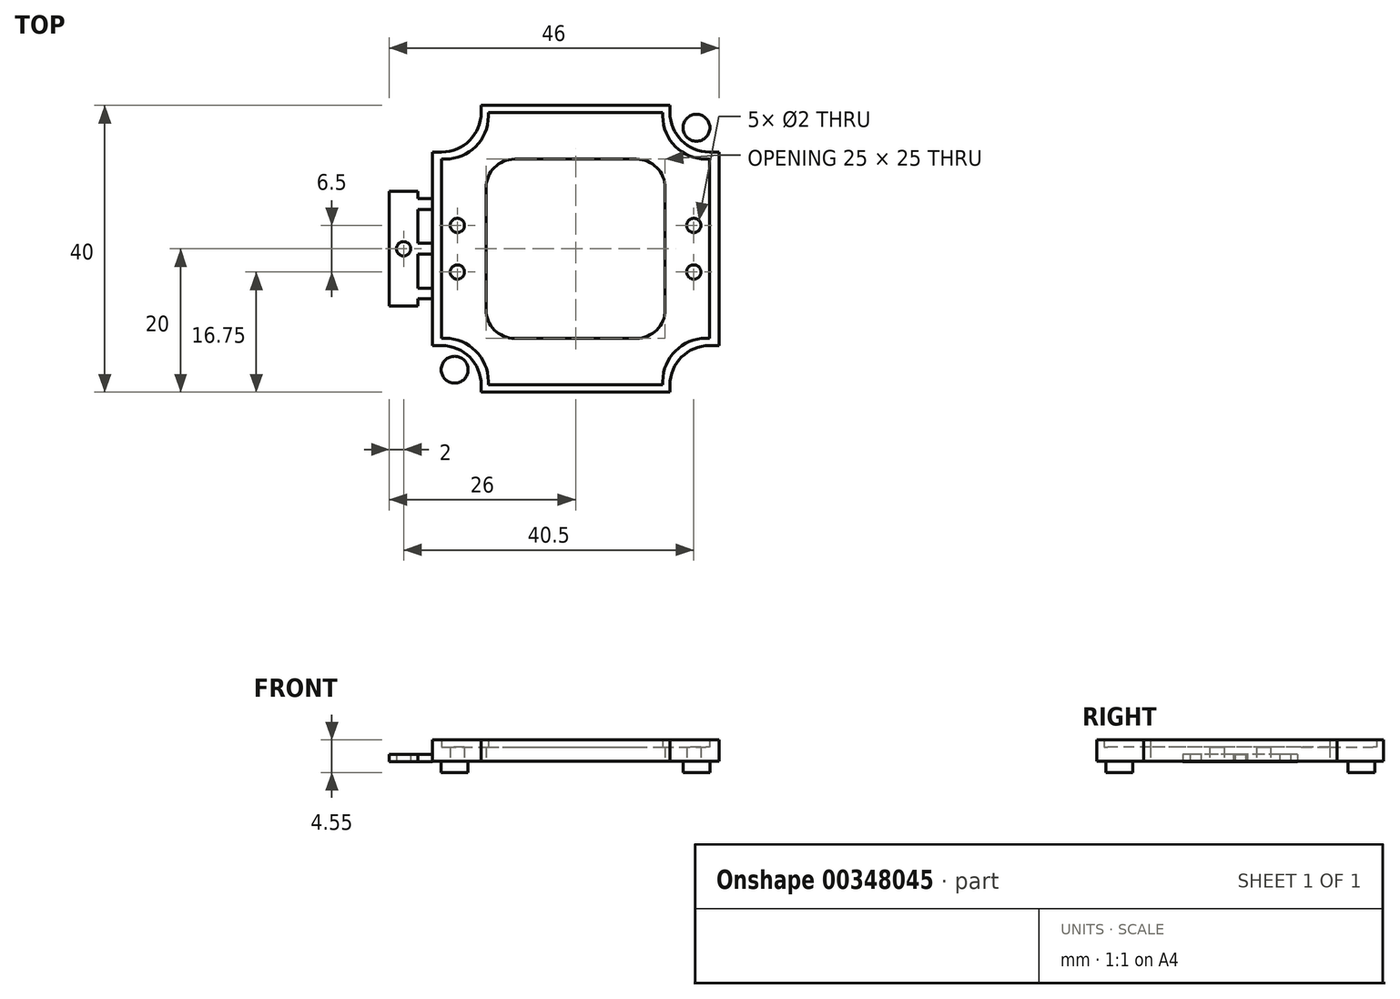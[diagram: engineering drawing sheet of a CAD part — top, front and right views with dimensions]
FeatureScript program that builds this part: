
annotation { "Feature Type Name" : "Feature", "Feature Type Description" : "" }
export const myFeature = defineFeature(function(context is Context, id is Id, definition is map)
    precondition{}
    {
        {
            var Q0;
            Q0=qCreatedBy(makeId("Top.planeOp"),FACE);
            var sketch = newSketch(context, id + "F0", { "sketchPlane" : qUnion([Q0])});
            skLineSegment(sketch, "E0.bottom", {"start": v(-20, 23) * mm, "end": v(20, 23) * mm});
            skLineSegment(sketch, "E0.top", {"start": v(-20, -23) * mm, "end": v(20, -23) * mm});
            skLineSegment(sketch, "E0.left", {"start": v(-20, 23) * mm, "end": v(-20, -23) * mm});
            skLineSegment(sketch, "E0.right", {"start": v(20, 23) * mm, "end": v(20, -23) * mm});
            skPoint(sketch, "E0.middle", {"position": v(0, 0) * mm});
            skLineSegment(sketch, "E1.bottom", {"start": v(-20, 7) * mm, "end": v(-22, 7) * mm});
            skLineSegment(sketch, "E1.top", {"start": v(-20, 5.5) * mm, "end": v(-22, 5.5) * mm});
            skLineSegment(sketch, "E1.left", {"start": v(-20, 7) * mm, "end": v(-20, 5.5) * mm});
            skLineSegment(sketch, "E2.bottom", {"start": v(-20, 0.75) * mm, "end": v(-22, 0.75) * mm});
            skLineSegment(sketch, "E2.top", {"start": v(-20, -0.75) * mm, "end": v(-22, -0.75) * mm});
            skLineSegment(sketch, "E2.left", {"start": v(-20, 0.75) * mm, "end": v(-20, -0.75) * mm});
            skLineSegment(sketch, "E3.MirrorCS", {"start": v(-20, -5.5) * mm, "end": v(-22, -5.5) * mm});
            skLineSegment(sketch, "E4.MirrorCS", {"start": v(-20, -7) * mm, "end": v(-22, -7) * mm});
            skLineSegment(sketch, "E5.bottom", {"start": v(-26, 8) * mm, "end": v(-22, 8) * mm});
            skLineSegment(sketch, "E5.top", {"start": v(-26, -8) * mm, "end": v(-22, -8) * mm});
            skLineSegment(sketch, "E5.left", {"start": v(-26, 8) * mm, "end": v(-26, -8) * mm});
            skLineSegment(sketch, "E5.right", {"start": v(-22, 8) * mm, "end": v(-22, 7) * mm});
            skCircle(sketch, "E6", {"center": v(-24, 0) * mm, "radius": 1 * mm});
            skLineSegment(sketch, "E7.MirrorCS", {"start": v(22, 0.75) * mm, "end": v(22, -0.75) * mm});
            skLineSegment(sketch, "E8.MirrorCS", {"start": v(20, 0.75) * mm, "end": v(20, -0.75) * mm});
            skLineSegment(sketch, "E9.MirrorCS", {"start": v(20, 7) * mm, "end": v(20, 5.5) * mm});
            skLineSegment(sketch, "E10.MirrorCS", {"start": v(22, 8) * mm, "end": v(22, 7) * mm});
            skLineSegment(sketch, "E11.MirrorCS", {"start": v(26, 8) * mm, "end": v(26, -8) * mm});
            skCircle(sketch, "E12.MirrorC", {"center": v(24, 0) * mm, "radius": 1 * mm});
            skLineSegment(sketch, "E13.MirrorCS", {"start": v(20, -0.75) * mm, "end": v(22, -0.75) * mm});
            skLineSegment(sketch, "E14.MirrorCS", {"start": v(26, -8) * mm, "end": v(22, -8) * mm});
            skLineSegment(sketch, "E15.MirrorCS", {"start": v(20, -5.5) * mm, "end": v(22, -5.5) * mm});
            skLineSegment(sketch, "E16.MirrorCS", {"start": v(20, 0.75) * mm, "end": v(22, 0.75) * mm});
            skLineSegment(sketch, "E17.MirrorCS", {"start": v(20, 7) * mm, "end": v(22, 7) * mm});
            skLineSegment(sketch, "E18.MirrorCS", {"start": v(20, -7) * mm, "end": v(22, -7) * mm});
            skLineSegment(sketch, "E19.MirrorCS", {"start": v(20, 5.5) * mm, "end": v(22, 5.5) * mm});
            skLineSegment(sketch, "E20.MirrorCS", {"start": v(26, 8) * mm, "end": v(22, 8) * mm});
            skLineSegment(sketch, "E21.trimOffspring", {"start": v(-22, 5.5) * mm, "end": v(-22, -5.5) * mm});
            skLineSegment(sketch, "E22.trimOffspring", {"start": v(-22, -7) * mm, "end": v(-22, -8) * mm});
            skPoint(sketch, "E23.MirrorCS.start.orphan", {"position": v(-22, -7) * mm});
            skLineSegment(sketch, "E24.trimOffspring", {"start": v(22, 5.5) * mm, "end": v(22, -5.5) * mm});
            skPoint(sketch, "E25.MirrorCS.end.orphan", {"position": v(22, -5.5) * mm});
            skPoint(sketch, "E25.MirrorCS.start.orphan", {"position": v(22, -7) * mm});
            skLineSegment(sketch, "E26.trimOffspring", {"start": v(22, -7) * mm, "end": v(22, -8) * mm});
            skSolve(sketch);
        }
        {
            var Q0;
            Q0=makeQuery(id+"F0.imprint","IMPRINT",FACE,{"disambiguationData":[TD([[makeQuery(id+"F0.imprint","IMPRINT",EDGE,{"derivedFrom":sQuery(id+"F0.wireOp",EDGE,"E0.bottom")}),-1.0]])]});
            extrude(context, id + "F1", {"entities" : qUnion([Q0]), "depth" : 1.55 * mm});
        }
        {
            var Q0;
            Q0=makeQuery(id+"F1.opExtrude","CAP_FACE",FACE,{"disambiguationData":[OSD([sQuery(id+"F0.wireOp",EDGE,"E0.bottom"),sQuery(id+"F0.wireOp",EDGE,"E0.top"),sQuery(id+"F0.wireOp",EDGE,"E0.left"),sQuery(id+"F0.wireOp",EDGE,"E0.right")])],"isStart":false});
            var sketch = newSketch(context, id + "F2", { "sketchPlane" : qUnion([Q0])});
            skLineSegment(sketch, "E27.bottom", {"start": v(-13.17, 20) * mm, "end": v(13.17, 20) * mm});
            skLineSegment(sketch, "E27.top", {"start": v(-13.17, -20) * mm, "end": v(13.17, -20) * mm});
            skLineSegment(sketch, "E27.left", {"start": v(-20, 13.5) * mm, "end": v(-20, -13.5) * mm});
            skLineSegment(sketch, "E27.right", {"start": v(20, 13.5) * mm, "end": v(20, -13.5) * mm});
            skPoint(sketch, "E27.middle", {"position": v(0, 0) * mm});
            skLineSegment(sketch, "E28.top", {"start": v(20, 13.5) * mm, "end": v(18.67, 13.5) * mm});
            skLineSegment(sketch, "E28.right", {"start": v(13.17, 20) * mm, "end": v(13.17, 19) * mm});
            skPoint(sketch, "E29.visualSharp", {"position": v(13.17, 13.5) * mm});
            skArc(sketch, "E29.filletArc", {"start": v(13.17, 19) * mm, "mid": v(14.78, 15.11) * mm, "end": v(18.67, 13.5) * mm});
            skLineSegment(sketch, "E30.MirrorCS", {"start": v(-13.17, 20) * mm, "end": v(-13.17, 19) * mm});
            skArc(sketch, "E31.MirrorCS", {"start": v(-13.17, 19) * mm, "mid": v(-14.78, 15.11) * mm, "end": v(-18.67, 13.5) * mm});
            skLineSegment(sketch, "E32.MirrorCS", {"start": v(-20, 13.5) * mm, "end": v(-18.67, 13.5) * mm});
            skArc(sketch, "E33.MirrorCS", {"start": v(-13.17, -19) * mm, "mid": v(-14.78, -15.11) * mm, "end": v(-18.67, -13.5) * mm});
            skLineSegment(sketch, "E34.MirrorCS", {"start": v(-20, -13.5) * mm, "end": v(-18.67, -13.5) * mm});
            skLineSegment(sketch, "E35.MirrorCS", {"start": v(-13.17, -20) * mm, "end": v(-13.17, -19) * mm});
            skLineSegment(sketch, "E36.MirrorCS", {"start": v(20, -13.5) * mm, "end": v(18.67, -13.5) * mm});
            skArc(sketch, "E37.MirrorCS", {"start": v(13.17, -19) * mm, "mid": v(14.78, -15.11) * mm, "end": v(18.67, -13.5) * mm});
            skLineSegment(sketch, "E38.MirrorCS", {"start": v(13.17, -20) * mm, "end": v(13.17, -19) * mm});
            skPoint(sketch, "E39.orphan", {"position": v(-20, 20) * mm});
            skLineSegment(sketch, "E40.bottom", {"start": v(-12.17, 19) * mm, "end": v(12.17, 19) * mm});
            skLineSegment(sketch, "E40.top", {"start": v(-12.17, -19) * mm, "end": v(12.17, -19) * mm});
            skLineSegment(sketch, "E40.left", {"start": v(-18.67, 12.5) * mm, "end": v(-18.67, -12.5) * mm});
            skLineSegment(sketch, "E41.top", {"start": v(-18.67, 12.5) * mm, "end": v(-18.17, 12.5) * mm});
            skLineSegment(sketch, "E41.right", {"start": v(-12.17, 19) * mm, "end": v(-12.17, 18.5) * mm});
            skPoint(sketch, "E42.visualSharp", {"position": v(-12.17, 12.5) * mm});
            skArc(sketch, "E42.filletArc", {"start": v(-18.17, 12.5) * mm, "mid": v(-13.93, 14.26) * mm, "end": v(-12.17, 18.5) * mm});
            skArc(sketch, "E43.MirrorCS", {"start": v(18.17, 12.5) * mm, "mid": v(13.93, 14.26) * mm, "end": v(12.17, 18.5) * mm});
            skLineSegment(sketch, "E44.MirrorCS", {"start": v(12.17, 19) * mm, "end": v(12.17, 18.5) * mm});
            skLineSegment(sketch, "E45.MirrorCS", {"start": v(18.67, 12.5) * mm, "end": v(18.17, 12.5) * mm});
            skArc(sketch, "E46.MirrorCS", {"start": v(18.17, -12.5) * mm, "mid": v(13.93, -14.26) * mm, "end": v(12.17, -18.5) * mm});
            skArc(sketch, "E47.MirrorCS", {"start": v(-18.17, -12.5) * mm, "mid": v(-13.93, -14.26) * mm, "end": v(-12.17, -18.5) * mm});
            skLineSegment(sketch, "E48.MirrorCS", {"start": v(-12.17, -19) * mm, "end": v(-12.17, -18.5) * mm});
            skLineSegment(sketch, "E49.MirrorCS", {"start": v(-18.67, -12.5) * mm, "end": v(-18.17, -12.5) * mm});
            skLineSegment(sketch, "E50.MirrorCS", {"start": v(18.67, -12.5) * mm, "end": v(18.17, -12.5) * mm});
            skLineSegment(sketch, "E51.MirrorCS", {"start": v(12.17, -19) * mm, "end": v(12.17, -18.5) * mm});
            skLineSegment(sketch, "E52.trimOffspring", {"start": v(18.67, 12.5) * mm, "end": v(18.67, -12.5) * mm});
            skPoint(sketch, "E40.right.start.orphan", {"position": v(19, 19) * mm});
            skCircle(sketch, "E53", {"center": v(-16.5, 3.25) * mm, "radius": 1 * mm});
            skCircle(sketch, "E54.MirrorC", {"center": v(-16.5, -3.25) * mm, "radius": 1 * mm});
            skCircle(sketch, "E55.MirrorC", {"center": v(16.5, -3.25) * mm, "radius": 1 * mm});
            skCircle(sketch, "E56.MirrorC", {"center": v(16.5, 3.25) * mm, "radius": 1 * mm});
            skLineSegment(sketch, "E57.bottom", {"start": v(-9.17, -18) * mm, "end": v(-9.67, -18) * mm});
            skLineSegment(sketch, "E57.top", {"start": v(-9.17, -14.5) * mm, "end": v(-9.67, -14.5) * mm});
            skLineSegment(sketch, "E57.left", {"start": v(-9.17, -18) * mm, "end": v(-9.17, -14.5) * mm});
            skLineSegment(sketch, "E57.right", {"start": v(-9.67, -18) * mm, "end": v(-9.67, -14.5) * mm});
            skLineSegment(sketch, "E58.bottom", {"start": v(-11.17, -15.98) * mm, "end": v(-7.67, -15.98) * mm});
            skLineSegment(sketch, "E58.top", {"start": v(-11.17, -16.48) * mm, "end": v(-7.67, -16.48) * mm});
            skLineSegment(sketch, "E58.left", {"start": v(-11.17, -15.98) * mm, "end": v(-11.17, -16.48) * mm});
            skLineSegment(sketch, "E58.right", {"start": v(-7.67, -15.98) * mm, "end": v(-7.67, -16.48) * mm});
            skPoint(sketch, "E58.middle", {"position": v(-9.42, -16.23) * mm});
            skLineSegment(sketch, "E59.bottom", {"start": v(-8.5, 12.5) * mm, "end": v(8.5, 12.5) * mm});
            skLineSegment(sketch, "E59.top", {"start": v(-8.5, -12.5) * mm, "end": v(8.5, -12.5) * mm});
            skLineSegment(sketch, "E59.left", {"start": v(-12.5, 8.5) * mm, "end": v(-12.5, -8.5) * mm});
            skLineSegment(sketch, "E59.right", {"start": v(12.5, 8.5) * mm, "end": v(12.5, -8.5) * mm});
            skPoint(sketch, "E60.visualSharp", {"position": v(-12.5, 12.5) * mm});
            skArc(sketch, "E60.filletArc", {"start": v(-8.5, 12.5) * mm, "mid": v(-11.33, 11.33) * mm, "end": v(-12.5, 8.5) * mm});
            skPoint(sketch, "E61.visualSharp", {"position": v(12.5, -12.5) * mm});
            skArc(sketch, "E61.filletArc", {"start": v(8.5, -12.5) * mm, "mid": v(11.33, -11.33) * mm, "end": v(12.5, -8.5) * mm});
            skPoint(sketch, "E62.visualSharp", {"position": v(-12.5, -12.5) * mm});
            skArc(sketch, "E62.filletArc", {"start": v(-12.5, -8.5) * mm, "mid": v(-11.33, -11.33) * mm, "end": v(-8.5, -12.5) * mm});
            skPoint(sketch, "E63.visualSharp", {"position": v(12.5, 12.5) * mm});
            skArc(sketch, "E63.filletArc", {"start": v(12.5, 8.5) * mm, "mid": v(11.33, 11.33) * mm, "end": v(8.5, 12.5) * mm});
            skSolve(sketch);
        }
        {
            var Q0;
            Q0=makeQuery(id+"F1.opExtrude","SWEPT_EDGE",EDGE,{"disambiguationData":[OSD([sQuery(id+"F0.wireOp",EDGE,"E0.bottom"),sQuery(id+"F0.wireOp",EDGE,"E0.left")])]});
            var Q1;
            Q1=makeQuery(id+"F1.opExtrude","SWEPT_EDGE",EDGE,{"disambiguationData":[OSD([sQuery(id+"F0.wireOp",EDGE,"E0.bottom"),sQuery(id+"F0.wireOp",EDGE,"E0.right")])]});
            var Q2;
            Q2=makeQuery(id+"F1.opExtrude","SWEPT_EDGE",EDGE,{"disambiguationData":[OSD([sQuery(id+"F0.wireOp",EDGE,"E0.top"),sQuery(id+"F0.wireOp",EDGE,"E0.right")])]});
            var Q3;
            Q3=makeQuery(id+"F1.opExtrude","SWEPT_EDGE",EDGE,{"disambiguationData":[OSD([sQuery(id+"F0.wireOp",EDGE,"E0.top"),sQuery(id+"F0.wireOp",EDGE,"E0.left")])]});
            chamfer(context, id + "F3", {"entities" : qUnion([Q0, Q1, Q2, Q3]), "width" : 4 * mm, "tangentPropagation" : true});
        }
        {
            var Q0;
            Q0=makeQuery(id+"F1.opExtrude","CAP_FACE",FACE,{"disambiguationData":[OSD([sQuery(id+"F0.wireOp",EDGE,"E0.bottom"),sQuery(id+"F0.wireOp",EDGE,"E0.top"),sQuery(id+"F0.wireOp",EDGE,"E0.left"),sQuery(id+"F0.wireOp",EDGE,"E0.right")])],"isStart":false});
            var sketch = newSketch(context, id + "F4", { "sketchPlane" : qUnion([Q0])});
            skCircle(sketch, "E64", {"center": v(-16.87, 16.88) * mm, "radius": 1.88 * mm});
            skCircle(sketch, "E65.MirrorC", {"center": v(16.87, 16.88) * mm, "radius": 1.88 * mm});
            skCircle(sketch, "E66.MirrorC", {"center": v(16.87, -16.88) * mm, "radius": 1.88 * mm});
            skCircle(sketch, "E67.MirrorC", {"center": v(-16.87, -16.88) * mm, "radius": 1.88 * mm});
            skSolve(sketch);
        }
        {
            var Q0;
            Q0=makeQuery(id+"F4.imprint","IMPRINT",FACE,{"disambiguationData":[TD([[makeQuery(id+"F4.imprint","IMPRINT",EDGE,{"derivedFrom":sQuery(id+"F4.wireOp",EDGE,"E67.MirrorC")}),-1.0]])]});
            var Q1;
            Q1=makeQuery(id+"F4.imprint","IMPRINT",FACE,{"disambiguationData":[TD([[makeQuery(id+"F4.imprint","IMPRINT",EDGE,{"derivedFrom":sQuery(id+"F4.wireOp",EDGE,"E66.MirrorC")}),1.0]])]});
            var Q2;
            Q2=makeQuery(id+"F4.imprint","IMPRINT",FACE,{"disambiguationData":[TD([[makeQuery(id+"F4.imprint","IMPRINT",EDGE,{"derivedFrom":sQuery(id+"F4.wireOp",EDGE,"E65.MirrorC")}),-1.0]])]});
            var Q3;
            Q3=makeQuery(id+"F4.imprint","IMPRINT",FACE,{"disambiguationData":[TD([[makeQuery(id+"F4.imprint","IMPRINT",EDGE,{"derivedFrom":sQuery(id+"F4.wireOp",EDGE,"E64")}),1.0]])]});
            extrude(context, id + "F5", {"entities" : qUnion([Q0, Q1, Q2, Q3]), "operationType" : NewBodyOperationType.REMOVE, "oppositeDirection" : true, "depth" : 4 * mm});
        }
        {
            var Q0;
            Q0=makeQuery(id+"F2.imprint","IMPRINT",FACE,{"disambiguationData":[TD([[makeQuery(id+"F2.imprint","IMPRINT",EDGE,{"derivedFrom":sQuery(id+"F2.wireOp",EDGE,"E27.bottom")}),-1.0]])]});
            extrude(context, id + "F6", {"entities" : qUnion([Q0]), "depth" : 3 * mm});
        }
        {
            var Q0;
            Q0=makeQuery(id+"F2.imprint","IMPRINT",FACE,{"disambiguationData":[TD([[makeQuery(id+"F2.imprint","IMPRINT",EDGE,{"derivedFrom":sQuery(id+"F2.wireOp",EDGE,"E40.bottom")}),-1.0]])]});
            var Q1;
            {var subQ5=sQuery(id+"F2.wireOp",EDGE,"E58.right");Q1=makeQuery(id+"F2.imprint","IMPRINT",FACE,{"disambiguationData":[TD([[makeQuery(id+"F2.imprint","IMPRINT",EDGE,{"derivedFrom":subQ5}),-1.0]])]});}
            var Q2;
            {var subQ5=sQuery(id+"F2.wireOp",EDGE,"E58.left");Q2=makeQuery(id+"F2.imprint","IMPRINT",FACE,{"disambiguationData":[TD([[makeQuery(id+"F2.imprint","IMPRINT",EDGE,{"derivedFrom":subQ5}),1.0]])]});}
            var Q3;
            {var subQ0=sQuery(id+"F2.wireOp",EDGE,"E57.bottom");Q3=makeQuery(id+"F2.imprint","IMPRINT",FACE,{"disambiguationData":[TD([[makeQuery(id+"F2.imprint","IMPRINT",EDGE,{"derivedFrom":subQ0}),-1.0]])]});}
            var Q4;
            {var subQ0=sQuery(id+"F2.wireOp",EDGE,"E57.top");Q4=makeQuery(id+"F2.imprint","IMPRINT",FACE,{"disambiguationData":[TD([[makeQuery(id+"F2.imprint","IMPRINT",EDGE,{"derivedFrom":subQ0}),1.0]])]});}
            var Q5;
            {var subQ0=sQuery(id+"F2.wireOp",EDGE,"E58.top");var subQ1=sQuery(id+"F2.wireOp",EDGE,"E57.left");var subQ2=makeQuery(id+"F2.imprint","INTERSECT",VERTEX,{"derivedFrom":[subQ1,subQ0]});Q5=makeQuery(id+"F2.imprint","IMPRINT",FACE,{"disambiguationData":[TD([[makeQuery(id+"F2.imprint","IMPRINT",EDGE,{"disambiguationData":[TD([[subQ2,-1.0]])],"derivedFrom":subQ1}),1.0]])]});}
            extrude(context, id + "F7", {"entities" : qUnion([Q0, Q1, Q2, Q3, Q4, Q5]), "operationType" : NewBodyOperationType.ADD, "depth" : 2 * mm});
        }
        {
            var Q0;
            Q0=makeQuery(id+"F2.imprint","IMPRINT",FACE,{"disambiguationData":[TD([[makeQuery(id+"F2.imprint","IMPRINT",EDGE,{"derivedFrom":sQuery(id+"F2.wireOp",EDGE,"E59.bottom")}),-1.0]])]});
            extrude(context, id + "F8", {"entities" : qUnion([Q0]), "depth" : 2 * mm});
        }
        {
            var Q0;
            Q0=makeQuery(id+"F0.imprint","IMPRINT",FACE,{"disambiguationData":[TD([[makeQuery(id+"F0.imprint","IMPRINT",EDGE,{"derivedFrom":sQuery(id+"F0.wireOp",EDGE,"E1.bottom")}),1.0]])]});
            var Q1;
            Q1=makeQuery(id+"F0.imprint","IMPRINT",FACE,{"disambiguationData":[TD([[makeQuery(id+"F0.imprint","IMPRINT",EDGE,{"derivedFrom":sQuery(id+"F0.wireOp",EDGE,"E9.MirrorCS")}),1.0]])]});
            var Q2;
            Q2=makeQuery(id+"F0.imprint","IMPRINT",FACE,{"disambiguationData":[TD([[makeQuery(id+"F0.imprint","IMPRINT",EDGE,{"derivedFrom":sQuery(id+"F0.wireOp",EDGE,"E8.MirrorCS")}),1.0]])]});
            var Q3;
            {var subQ0=sQuery(id+"F0.wireOp",EDGE,"E2.bottom");Q3=makeQuery(id+"F0.imprint","IMPRINT",FACE,{"disambiguationData":[TD([[makeQuery(id+"F0.imprint","IMPRINT",EDGE,{"derivedFrom":subQ0}),1.0]])]});}
            extrude(context, id + "F9", {"entities" : qUnion([Q0, Q1, Q2, Q3]), "operationType" : NewBodyOperationType.ADD, "depth" : 2.5 * mm, "hasSecondDirection" : true, "secondDirectionOppositeDirection" : false, "secondDirectionDepth" : 1.5 * mm});
        }
    });
